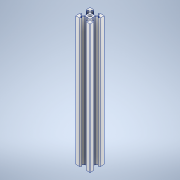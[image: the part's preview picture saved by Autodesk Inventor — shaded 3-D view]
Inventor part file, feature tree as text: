
AUTODESK INVENTOR PART (.ipt)
format: ipt  version: 2021 (Build 250183000, 183)  size: 236,032 bytes
history: native  units: mm
features: sketch x3, extrude x2, fillet x2, other x1, pattern_circular x1, hole x1, projected_geometry x1
ambient origin geometry x8: Origin, YZ Plane, XZ Plane, XY Plane, X Axis, Y Axis, Z Axis, Center Point
bodies: Body1 (feature_tree)
feature tree (11):
  other  "實體1"
  extrude  "擠出1"  Depth=20.0mm
  extrude  "擠出2"  Depth=20.0mm
  fillet  "圓角1"  Radius=180.0mm
  pattern_circular  "環形陣列1"  [2 undecoded]
  hole  "孔1"  [1 undecoded]
  fillet  "圓角2"  Radius=6.2mm
  sketch  "草圖1"
  sketch  "草圖2"
  projected_geometry  "投影迴路1"
  sketch  "草圖3"
note: 3 required parameter values undecoded (feature->parameter linkage not recoverable at this tier; creation-order binding heuristic only, values carry confidence <= 0.55)
